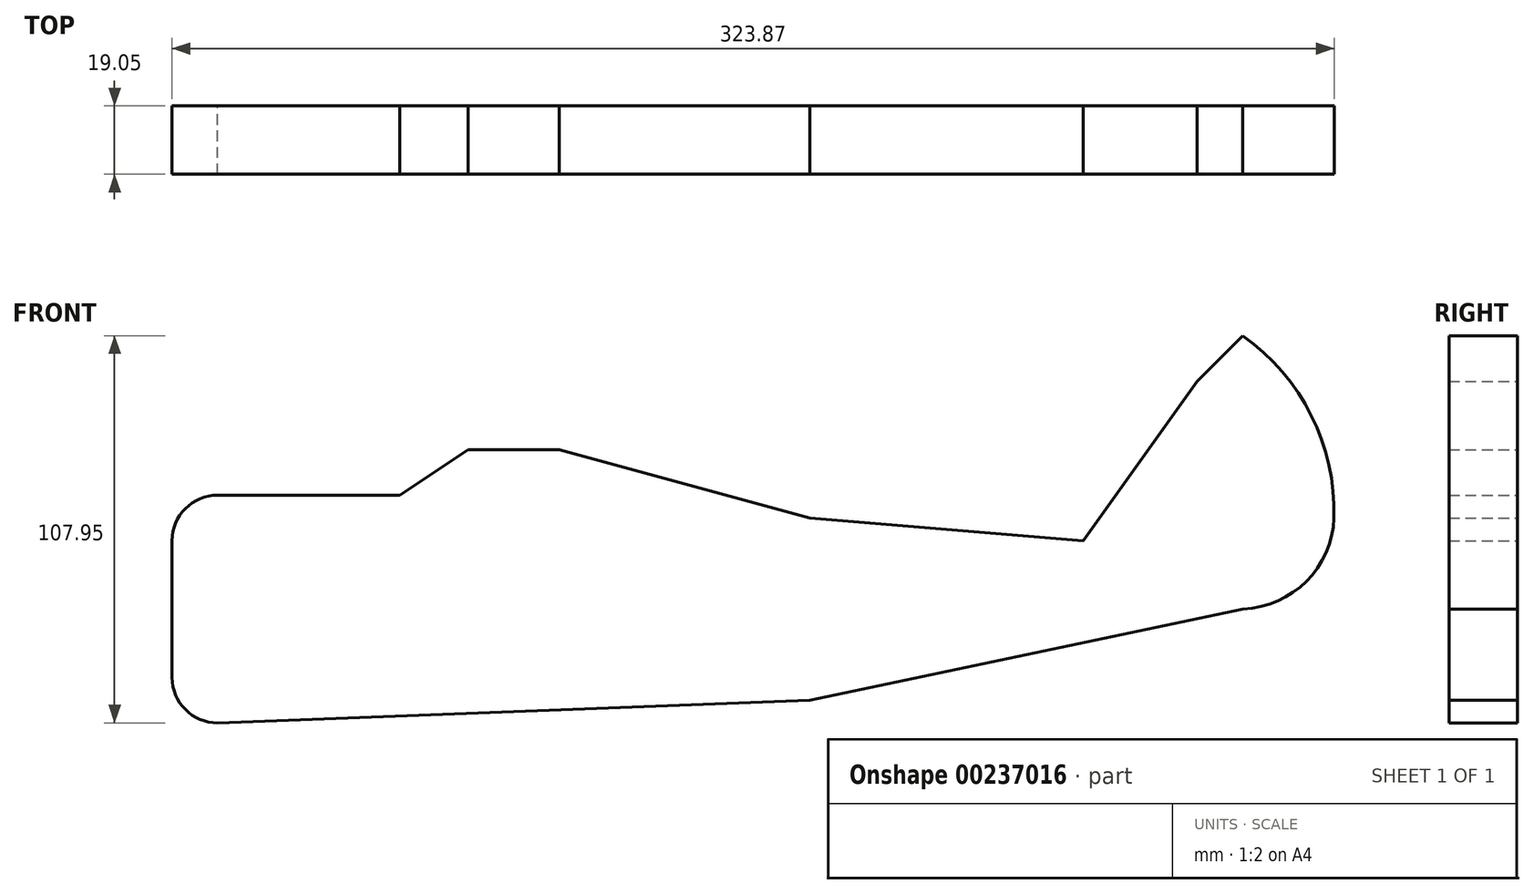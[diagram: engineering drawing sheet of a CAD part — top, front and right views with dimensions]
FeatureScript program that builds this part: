
annotation { "Feature Type Name" : "Feature", "Feature Type Description" : "" }
export const myFeature = defineFeature(function(context is Context, id is Id, definition is map)
    precondition{}
    {
        {
            var Q0;
            Q0=qCreatedBy(makeId("Front.planeOp"),FACE);
            var sketch = newSketch(context, id + "F0", { "sketchPlane" : qUnion([Q0])});
            skPoint(sketch, "E0.middle", {"position": v(0, 0) * mm});
            skArc(sketch, "E1", {"start": v(-165.1, -38.1) * mm, "mid": v(-161.38, -47.08) * mm, "end": v(-152.4, -50.8) * mm});
            skLineSegment(sketch, "E2", {"start": v(-165.1, -38.1) * mm, "end": v(-165.1, 0) * mm});
            skArc(sketch, "E3", {"start": v(-152.4, 12.7) * mm, "mid": v(-161.38, 8.98) * mm, "end": v(-165.1, 0) * mm});
            skLineSegment(sketch, "E4", {"start": v(-152.4, 12.7) * mm, "end": v(-101.6, 12.7) * mm});
            skLineSegment(sketch, "E5", {"start": v(-101.6, 12.7) * mm, "end": v(-82.55, 25.4) * mm});
            skLineSegment(sketch, "E6", {"start": v(-82.55, 25.4) * mm, "end": v(-57.15, 25.4) * mm});
            skLineSegment(sketch, "E7", {"start": v(-57.15, 25.4) * mm, "end": v(12.7, 6.35) * mm});
            skLineSegment(sketch, "E8", {"start": v(12.7, 6.35) * mm, "end": v(88.9, 0) * mm});
            skLineSegment(sketch, "E9", {"start": v(88.9, 0) * mm, "end": v(120.65, 44.45) * mm});
            skLineSegment(sketch, "E10", {"start": v(120.65, 44.45) * mm, "end": v(133.35, 57.15) * mm});
            skArc(sketch, "E11", {"start": v(158.75, 6.35) * mm, "mid": v(152.4, 34.93) * mm, "end": v(133.35, 57.15) * mm});
            skArc(sketch, "E12", {"start": v(133.35, -19.05) * mm, "mid": v(151.04, -11.34) * mm, "end": v(158.75, 6.35) * mm});
            skLineSegment(sketch, "E13", {"start": v(133.35, -19.05) * mm, "end": v(12.7, -44.45) * mm});
            skLineSegment(sketch, "E14", {"start": v(12.7, -44.45) * mm, "end": v(-152.4, -50.8) * mm});
            skSolve(sketch);
        }
        {
            var Q0;
            Q0=makeQuery(id+"F0.imprint","IMPRINT",FACE,{"disambiguationData":[TD([[makeQuery(id+"F0.imprint","IMPRINT",EDGE,{"derivedFrom":sQuery(id+"F0.wireOp",EDGE,"E1")}),1.0]])]});
            extrude(context, id + "F1", {"entities" : qUnion([Q0]), "depth" : 19.05 * mm});
        }
    });
